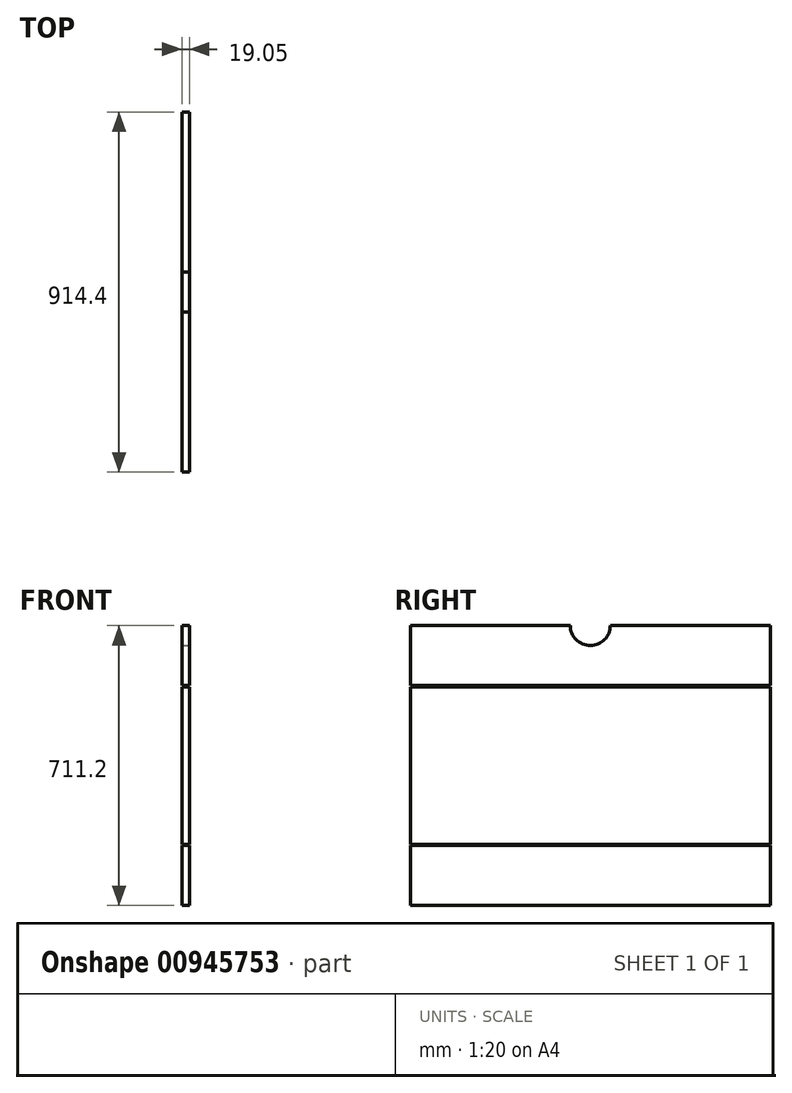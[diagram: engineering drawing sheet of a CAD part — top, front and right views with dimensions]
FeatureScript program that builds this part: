
annotation { "Feature Type Name" : "Feature", "Feature Type Description" : "" }
export const myFeature = defineFeature(function(context is Context, id is Id, definition is map)
    precondition{}
    {
        {
            var Q0;
            Q0=qCreatedBy(makeId("Right.planeOp"),FACE);
            var sketch = newSketch(context, id + "F0", { "sketchPlane" : qUnion([Q0])});
            skLineSegment(sketch, "E0.bottom", {"start": v(457.2, 355.6) * mm, "end": v(-457.2, 355.6) * mm});
            skLineSegment(sketch, "E0.top", {"start": v(457.2, -355.6) * mm, "end": v(-457.2, -355.6) * mm});
            skLineSegment(sketch, "E0.left", {"start": v(457.2, 355.6) * mm, "end": v(457.2, -355.6) * mm});
            skLineSegment(sketch, "E0.right", {"start": v(-457.2, 355.6) * mm, "end": v(-457.2, -355.6) * mm});
            skPoint(sketch, "E0.middle", {"position": v(0, 0) * mm});
            skSolve(sketch);
        }
        {
            var Q0;
            Q0=makeQuery(id+"F0.imprint","IMPRINT",FACE,{"disambiguationData":[TD([[makeQuery(id+"F0.imprint","IMPRINT",EDGE,{"derivedFrom":sQuery(id+"F0.wireOp",EDGE,"E0.bottom")}),1.0]])]});
            extrude(context, id + "F1", {"entities" : qUnion([Q0]), "depth" : 19.05 * mm, "offsetDistance" : 25.4 * mm});
        }
        {
            var Q0;
            Q0=makeQuery(id+"F1.opExtrude","CAP_FACE",FACE,{"disambiguationData":[OSD([sQuery(id+"F0.wireOp",EDGE,"E0.bottom"),sQuery(id+"F0.wireOp",EDGE,"E0.top"),sQuery(id+"F0.wireOp",EDGE,"E0.left"),sQuery(id+"F0.wireOp",EDGE,"E0.right")])],"isStart":false});
            var sketch = newSketch(context, id + "F2", { "sketchPlane" : qUnion([Q0])});
            skCircle(sketch, "E1", {"center": v(0, 355.6) * mm, "radius": 50.8 * mm});
            skSolve(sketch);
        }
        {
            var Q0;
            {var subQ0=sQuery(id+"F2.wireOp",EDGE,"E1");var subQ1=makeQuery(id+"F1.opExtrude","CAP_EDGE",EDGE,{"disambiguationData":[OSD([sQuery(id+"F0.wireOp",EDGE,"E0.bottom")])],"isStart":false});var subQ2=makeQuery(id+"F2.imprint","INTERSECT",VERTEX,{"disambiguationData":[OD(0.0)],"derivedFrom":[subQ1,subQ0]});Q0=makeQuery(id+"F2.imprint","IMPRINT",FACE,{"disambiguationData":[TD([[makeQuery(id+"F2.imprint","IMPRINT",EDGE,{"disambiguationData":[TD([[subQ2,1.0]])],"derivedFrom":subQ0}),1.0]])]});}
            extrude(context, id + "F3", {"entities" : qUnion([Q0]), "operationType" : NewBodyOperationType.REMOVE, "oppositeDirection" : true, "depth" : 25.4 * mm, "offsetDistance" : 25.4 * mm});
        }
        {
            var Q0;
            Q0=makeQuery(id+"F1.opExtrude","CAP_FACE",FACE,{"disambiguationData":[OSD([sQuery(id+"F0.wireOp",EDGE,"E0.bottom"),sQuery(id+"F0.wireOp",EDGE,"E0.top"),sQuery(id+"F0.wireOp",EDGE,"E0.left"),sQuery(id+"F0.wireOp",EDGE,"E0.right")])],"isStart":false});
            var sketch = newSketch(context, id + "F4", { "sketchPlane" : qUnion([Q0])});
            skLineSegment(sketch, "E2.bottom", {"start": v(-457.2, 355.6) * mm, "end": v(457.2, 355.6) * mm});
            skLineSegment(sketch, "E2.top", {"start": v(-457.2, 203.2) * mm, "end": v(457.2, 203.2) * mm});
            skLineSegment(sketch, "E2.left", {"start": v(-457.2, 355.6) * mm, "end": v(-457.2, 203.2) * mm});
            skLineSegment(sketch, "E2.right", {"start": v(457.2, 355.6) * mm, "end": v(457.2, 203.2) * mm});
            skLineSegment(sketch, "E3.bottom", {"start": v(-457.2, -355.6) * mm, "end": v(457.2, -355.6) * mm});
            skLineSegment(sketch, "E3.top", {"start": v(-457.2, -203.2) * mm, "end": v(457.2, -203.2) * mm});
            skLineSegment(sketch, "E3.left", {"start": v(-457.2, -355.6) * mm, "end": v(-457.2, -203.2) * mm});
            skLineSegment(sketch, "E3.right", {"start": v(457.2, -355.6) * mm, "end": v(457.2, -203.2) * mm});
            skLineSegment(sketch, "E4.top", {"start": v(-457.2, -200.03) * mm, "end": v(457.2, -200.03) * mm});
            skLineSegment(sketch, "E4.left", {"start": v(-457.2, -203.2) * mm, "end": v(-457.2, -200.03) * mm});
            skLineSegment(sketch, "E4.right", {"start": v(457.2, -203.2) * mm, "end": v(457.2, -200.03) * mm});
            skLineSegment(sketch, "E5.top", {"start": v(-457.2, 200.02) * mm, "end": v(457.2, 200.02) * mm});
            skLineSegment(sketch, "E5.left", {"start": v(-457.2, 203.2) * mm, "end": v(-457.2, 200.02) * mm});
            skLineSegment(sketch, "E5.right", {"start": v(457.2, 203.2) * mm, "end": v(457.2, 200.02) * mm});
            skSolve(sketch);
        }
        {
            var Q0;
            Q0=makeQuery(id+"F4.imprint","IMPRINT",FACE,{"disambiguationData":[TD([[makeQuery(id+"F4.imprint","IMPRINT",EDGE,{"derivedFrom":sQuery(id+"F4.wireOp",EDGE,"E2.top")}),-1.0]])]});
            var Q1;
            Q1=makeQuery(id+"F4.imprint","IMPRINT",FACE,{"disambiguationData":[TD([[makeQuery(id+"F4.imprint","IMPRINT",EDGE,{"derivedFrom":sQuery(id+"F4.wireOp",EDGE,"E3.top")}),1.0]])]});
            extrude(context, id + "F5", {"entities" : qUnion([Q0, Q1]), "operationType" : NewBodyOperationType.REMOVE, "oppositeDirection" : true, "depth" : 25.4 * mm, "offsetDistance" : 25.4 * mm});
        }
    });
